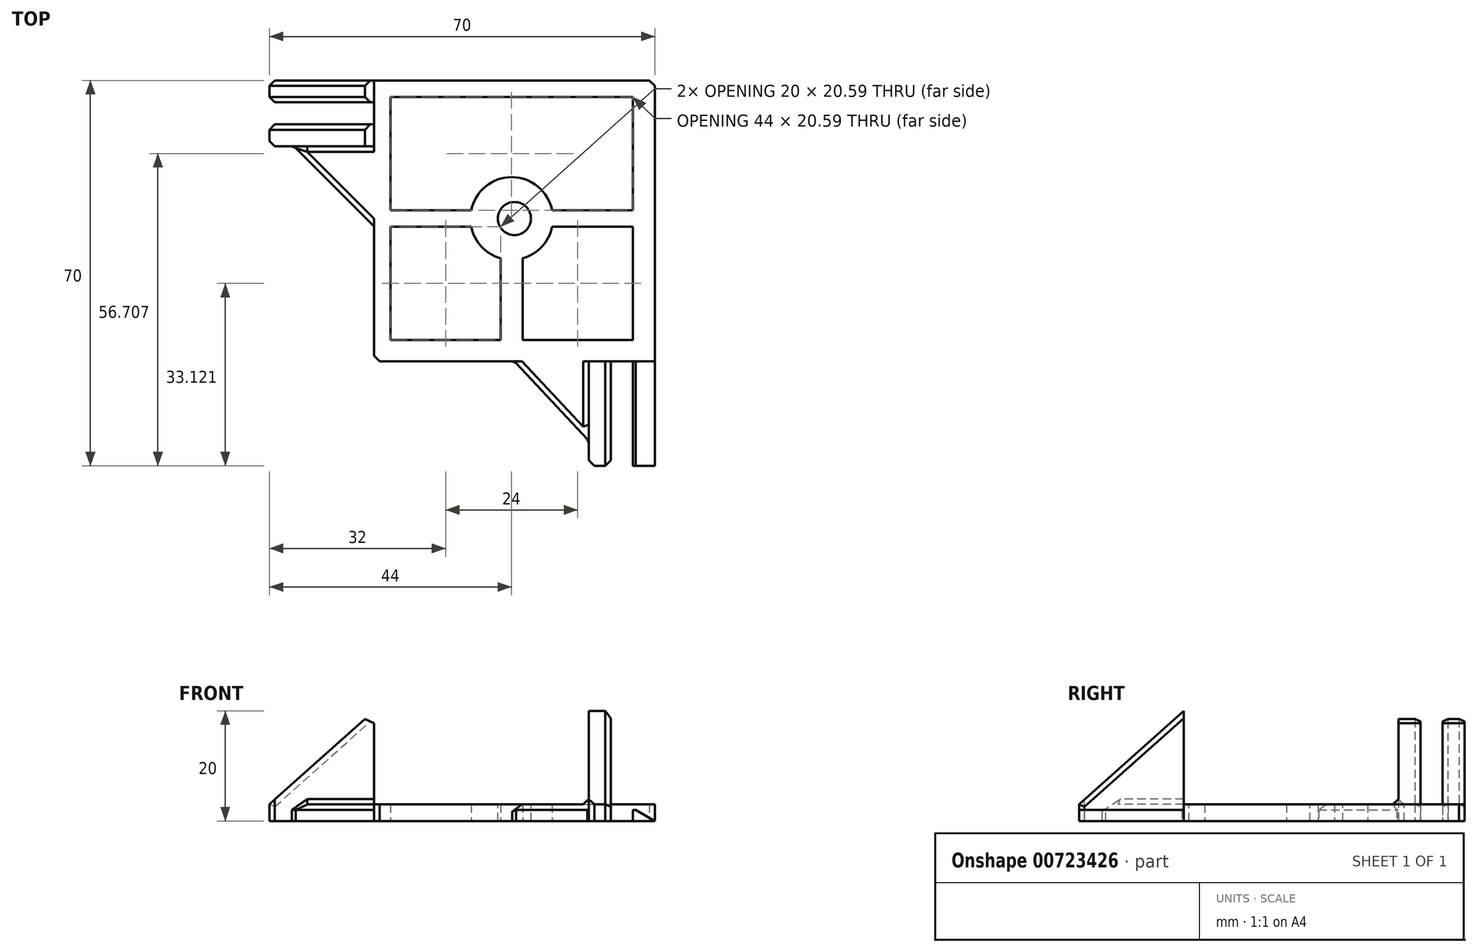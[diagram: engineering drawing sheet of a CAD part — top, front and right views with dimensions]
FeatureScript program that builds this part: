
annotation { "Feature Type Name" : "Feature", "Feature Type Description" : "" }
export const myFeature = defineFeature(function(context is Context, id is Id, definition is map)
    precondition{}
    {
        {
            var Q0;
            Q0=qCreatedBy(makeId("Top.planeOp"),FACE);
            var sketch = newSketch(context, id + "F0", { "sketchPlane" : qUnion([Q0])});
            skLineSegment(sketch, "E0.bottom", {"start": v(0, 0) * mm, "end": v(51, 0) * mm});
            skLineSegment(sketch, "E0.top", {"start": v(0, -51) * mm, "end": v(51, -51) * mm});
            skLineSegment(sketch, "E0.left", {"start": v(0, 0) * mm, "end": v(0, -51) * mm});
            skLineSegment(sketch, "E0.right", {"start": v(51, 0) * mm, "end": v(51, -51) * mm});
            skSolve(sketch);
        }
        {
            var Q0;
            Q0=qSketchRegion(id+"F0",true);
            extrude(context, id + "F1", {"entities" : qUnion([Q0]), "depth" : 3 * mm, "offsetDistance" : 25 * mm});
        }
        {
            var Q0;
            Q0=qCreatedBy(makeId("Top.planeOp"),FACE);
            var sketch = newSketch(context, id + "F2", { "sketchPlane" : qUnion([Q0])});
            skLineSegment(sketch, "E1", {"start": v(0, 0) * mm, "end": v(-19, 0) * mm});
            skLineSegment(sketch, "E2", {"start": v(-19, 0) * mm, "end": v(-19, -4) * mm});
            skLineSegment(sketch, "E3", {"start": v(-19, -4) * mm, "end": v(0, -4) * mm});
            skLineSegment(sketch, "E4", {"start": v(0, -4) * mm, "end": v(0, -8) * mm});
            skLineSegment(sketch, "E5", {"start": v(0, -8) * mm, "end": v(-19, -8) * mm});
            skLineSegment(sketch, "E6", {"start": v(-19, -8) * mm, "end": v(-19, -12) * mm});
            skLineSegment(sketch, "E7", {"start": v(-19, -12) * mm, "end": v(0, -12) * mm});
            skLineSegment(sketch, "E8", {"start": v(0, 0) * mm, "end": v(0, -12) * mm});
            skSolve(sketch);
        }
        {
            var Q0;
            Q0=qSketchRegion(id+"F2",true);
            extrude(context, id + "F3", {"entities" : qUnion([Q0]), "operationType" : NewBodyOperationType.ADD, "depth" : 20 * mm, "offsetDistance" : 25 * mm});
        }
        {
            var Q0;
            Q0=qCreatedBy(makeId("Top.planeOp"),FACE);
            var sketch = newSketch(context, id + "F4", { "sketchPlane" : qUnion([Q0])});
            skLineSegment(sketch, "E9", {"start": v(0, 0) * mm, "end": v(0, -11.5) * mm});
            skLineSegment(sketch, "E10", {"start": v(0, -11.5) * mm, "end": v(-15, -11.5) * mm});
            skLineSegment(sketch, "E11", {"start": v(0, -11.5) * mm, "end": v(0, -26.5) * mm});
            skLineSegment(sketch, "E12", {"start": v(0, -26.5) * mm, "end": v(-15, -11.5) * mm});
            skSolve(sketch);
        }
        {
            var Q0;
            Q0=makeQuery(id+"F4.imprint","IMPRINT",FACE,{"disambiguationData":[TD([[makeQuery(id+"F4.imprint","IMPRINT",EDGE,{"derivedFrom":sQuery(id+"F4.wireOp",EDGE,"E10")}),1.0]])]});
            extrude(context, id + "F5", {"entities" : qUnion([Q0]), "operationType" : NewBodyOperationType.ADD, "depth" : 3 * mm, "offsetDistance" : 25 * mm});
        }
        {
            var Q0;
            Q0=qCreatedBy(makeId("Top.planeOp"),FACE);
            var sketch = newSketch(context, id + "F6", { "sketchPlane" : qUnion([Q0])});
            skLineSegment(sketch, "E13", {"start": v(0, 0) * mm, "end": v(0, -51) * mm});
            skLineSegment(sketch, "E14", {"start": v(0, -51) * mm, "end": v(51, -51) * mm});
            skLineSegment(sketch, "E15", {"start": v(51, -51) * mm, "end": v(51, -70) * mm});
            skLineSegment(sketch, "E16", {"start": v(51, -70) * mm, "end": v(47, -70) * mm});
            skLineSegment(sketch, "E17", {"start": v(47, -70) * mm, "end": v(47, -51) * mm});
            skLineSegment(sketch, "E18", {"start": v(47, -51) * mm, "end": v(43, -51) * mm});
            skLineSegment(sketch, "E19", {"start": v(43, -51) * mm, "end": v(43, -70) * mm});
            skLineSegment(sketch, "E20", {"start": v(43, -70) * mm, "end": v(39, -70) * mm});
            skLineSegment(sketch, "E21", {"start": v(39, -70) * mm, "end": v(39, -51) * mm});
            skLineSegment(sketch, "E22", {"start": v(39, -51) * mm, "end": v(51, -51) * mm});
            skSolve(sketch);
        }
        {
            var Q0;
            Q0=qCreatedBy(makeId("Top.planeOp"),FACE);
            var sketch = newSketch(context, id + "F7", { "sketchPlane" : qUnion([Q0])});
            skLineSegment(sketch, "E23", {"start": v(0, 0) * mm, "end": v(0, -51) * mm});
            skLineSegment(sketch, "E24", {"start": v(0, -51) * mm, "end": v(51, -51) * mm});
            skLineSegment(sketch, "E25", {"start": v(51, -51) * mm, "end": v(39.5, -51) * mm});
            skLineSegment(sketch, "E26", {"start": v(39.5, -51) * mm, "end": v(39.5, -66) * mm});
            skLineSegment(sketch, "E27", {"start": v(39.5, -66) * mm, "end": v(25.5, -51) * mm});
            skLineSegment(sketch, "E28", {"start": v(25.5, -51) * mm, "end": v(39.5, -51) * mm});
            skSolve(sketch);
        }
        {
            var Q0;
            Q0=qSketchRegion(id+"F7",true);
            extrude(context, id + "F8", {"entities" : qUnion([Q0]), "operationType" : NewBodyOperationType.ADD, "depth" : 3 * mm, "offsetDistance" : 25 * mm});
        }
        {
            var Q0;
            Q0=makeQuery(id+"F8.opExtrude","CAP_EDGE",EDGE,{"disambiguationData":[OSD([sQuery(id+"F7.wireOp",EDGE,"E27")])],"isStart":false});
            chamfer(context, id + "F9", {"entities" : qUnion([Q0]), "width" : 1 * mm, "tangentPropagation" : true});
        }
        {
            var Q0;
            Q0=makeQuery(id+"F8.boolean.opBoolean","MERGE",FACE,{"derivedFrom":[makeQuery(id+"F5.boolean.opBoolean","MERGE",FACE,{"derivedFrom":[makeQuery(id+"F1.opExtrude","CAP_FACE",FACE,{"disambiguationData":[OSD([sQuery(id+"F0.wireOp",EDGE,"E0.bottom"),sQuery(id+"F0.wireOp",EDGE,"E0.top"),sQuery(id+"F0.wireOp",EDGE,"E0.left"),sQuery(id+"F0.wireOp",EDGE,"E0.right")])],"isStart":false}),makeQuery(id+"F5.opExtrude","CAP_FACE",FACE,{"disambiguationData":[OSD([sQuery(id+"F4.wireOp",EDGE,"E10"),sQuery(id+"F4.wireOp",EDGE,"E11"),sQuery(id+"F4.wireOp",EDGE,"E12")])],"isStart":false})]}),makeQuery(id+"F8.opExtrude","CAP_FACE",FACE,{"disambiguationData":[OSD([sQuery(id+"F7.wireOp",EDGE,"E26"),sQuery(id+"F7.wireOp",EDGE,"E27"),sQuery(id+"F7.wireOp",EDGE,"E28")])],"isStart":false})]});
            var sketch = newSketch(context, id + "F10", { "sketchPlane" : qUnion([Q0])});
            skCircle(sketch, "E29", {"center": v(25.5, -25.09) * mm, "radius": 3 * mm});
            skPoint(sketch, "E29.centerSnap0", {"position": v(25.5, 0) * mm});
            skSolve(sketch);
        }
        {
            var Q0;
            Q0=qSketchRegion(id+"F10",true);
            extrude(context, id + "F11", {"entities" : qUnion([Q0]), "operationType" : NewBodyOperationType.REMOVE, "oppositeDirection" : true, "depth" : 25 * mm, "offsetDistance" : 25 * mm});
        }
        {
            var Q0;
            {var subQ0=sQuery(id+"F6.wireOp",EDGE,"E19");Q0=makeQuery(id+"F6.imprint","IMPRINT",FACE,{"disambiguationData":[TD([[makeQuery(id+"F6.imprint","IMPRINT",EDGE,{"derivedFrom":subQ0}),-1.0]])]});}
            extrude(context, id + "F12", {"entities" : qUnion([Q0]), "operationType" : NewBodyOperationType.ADD, "depth" : 20 * mm, "offsetDistance" : 25 * mm});
        }
        {
            var Q0;
            Q0 = qSketchRegion(id + "F6", true);
            extrude(context, id + "F13", {"entities" : qUnion([Q0]), "operationType" : NewBodyOperationType.ADD, "depth" : 2 * mm, "offsetDistance" : 25 * mm});
        }
        {
            var Q0;
            Q0=makeQuery(id+"F13.opExtrude","CAP_EDGE",EDGE,{"disambiguationData":[OSD([sQuery(id+"F6.wireOp",EDGE,"E15")])],"isStart":false});
            chamfer(context, id + "F14", {"entities" : qUnion([Q0]), "chamferType" : ChamferType.OFFSET_ANGLE, "width" : 2 * mm, "oppositeDirection" : false, "angle" : 60 * degree});
        }
        {
            var Q0;
            Q0=qCreatedBy(makeId("Top.planeOp"),FACE);
            var sketch = newSketch(context, id + "F15", { "sketchPlane" : qUnion([Q0])});
            skCircle(sketch, "E30", {"center": v(25, -25.09) * mm, "radius": 7.5 * mm});
            skLineSegment(sketch, "E31", {"start": v(0, 0) * mm, "end": v(0, -3) * mm});
            skLineSegment(sketch, "E32", {"start": v(0, -3) * mm, "end": v(25, -3) * mm});
            skLineSegment(sketch, "E33", {"start": v(25, -3) * mm, "end": v(23, -3) * mm});
            skLineSegment(sketch, "E34", {"start": v(23, -3) * mm, "end": v(23, -17.86) * mm});
            skLineSegment(sketch, "E35", {"start": v(0, -3) * mm, "end": v(3, -3) * mm});
            skLineSegment(sketch, "E36", {"start": v(3, -3) * mm, "end": v(3, -25.09) * mm});
            skLineSegment(sketch, "E37", {"start": v(3, -25.09) * mm, "end": v(3, -23.59) * mm});
            skLineSegment(sketch, "E38", {"start": v(3, -23.59) * mm, "end": v(17.65, -23.59) * mm});
            skLineSegment(sketch, "E39", {"start": v(25, -25.09) * mm, "end": v(51, -25.09) * mm});
            skLineSegment(sketch, "E40", {"start": v(25, -25.09) * mm, "end": v(25, -51) * mm});
            skLineSegment(sketch, "E41.MirrorCS", {"start": v(3, -26.59) * mm, "end": v(17.65, -26.59) * mm});
            skLineSegment(sketch, "E42.MirrorCS", {"start": v(3, -47.17) * mm, "end": v(3, -25.09) * mm});
            skLineSegment(sketch, "E43.MirrorCS", {"start": v(0, -47.17) * mm, "end": v(25, -47.17) * mm});
            skLineSegment(sketch, "E44.MirrorCS", {"start": v(23, -47.17) * mm, "end": v(23, -32.31) * mm});
            skLineSegment(sketch, "E45.MirrorCS", {"start": v(27, -47.17) * mm, "end": v(27, -32.31) * mm});
            skLineSegment(sketch, "E46.MirrorCS", {"start": v(50, -47.17) * mm, "end": v(25, -47.17) * mm});
            skLineSegment(sketch, "E47.MirrorCS", {"start": v(47, -47.17) * mm, "end": v(47, -25.09) * mm});
            skLineSegment(sketch, "E48.MirrorCS", {"start": v(47, -26.59) * mm, "end": v(32.35, -26.59) * mm});
            skLineSegment(sketch, "E49.MirrorCS", {"start": v(47, -23.59) * mm, "end": v(32.35, -23.59) * mm});
            skLineSegment(sketch, "E50.MirrorCS", {"start": v(47, -3) * mm, "end": v(47, -25.09) * mm});
            skLineSegment(sketch, "E51.MirrorCS", {"start": v(50, -3) * mm, "end": v(25, -3) * mm});
            skLineSegment(sketch, "E52.MirrorCS", {"start": v(27, -3) * mm, "end": v(27, -17.86) * mm});
            skLineSegment(sketch, "E53", {"start": v(0, 0) * mm, "end": v(0, -47.17) * mm});
            skSolve(sketch);
        }
        {
            var Q0;
            {var subQ4=sQuery(id+"F15.wireOp",EDGE,"E49.MirrorCS");Q0=makeQuery(id+"F15.imprint","IMPRINT",FACE,{"disambiguationData":[TD([[makeQuery(id+"F15.imprint","IMPRINT",EDGE,{"derivedFrom":subQ4}),-1.0]])]});}
            var Q1;
            {var subQ4=sQuery(id+"F15.wireOp",EDGE,"E45.MirrorCS");Q1=makeQuery(id+"F15.imprint","IMPRINT",FACE,{"disambiguationData":[TD([[makeQuery(id+"F15.imprint","IMPRINT",EDGE,{"derivedFrom":subQ4}),-1.0]])]});}
            var Q2;
            {var subQ1=sQuery(id+"F15.wireOp",EDGE,"E41.MirrorCS");Q2=makeQuery(id+"F15.imprint","IMPRINT",FACE,{"disambiguationData":[TD([[makeQuery(id+"F15.imprint","IMPRINT",EDGE,{"derivedFrom":subQ1}),-1.0]])]});}
            var Q3;
            Q3=makeQuery(id+"F15.imprint","IMPRINT",FACE,{"disambiguationData":[TD([[makeQuery(id+"F15.imprint","IMPRINT",EDGE,{"derivedFrom":sQuery(id+"F15.wireOp",EDGE,"E32")}),-1.0]])]});
            extrude(context, id + "F16", {"entities" : qUnion([Q0, Q1, Q2, Q3]), "operationType" : NewBodyOperationType.REMOVE, "depth" : 25 * mm, "offsetDistance" : 25 * mm});
        }
        {
            var Q0;
            Q0=makeQuery(id+"F3.opExtrude","SWEPT_FACE",FACE,{"disambiguationData":[OSD([sQuery(id+"F2.wireOp",EDGE,"E7")])]});
            var sketch = newSketch(context, id + "F17", { "sketchPlane" : qUnion([Q0])});
            skLineSegment(sketch, "E54", {"start": v(-19, 20) * mm, "end": v(-19, 3) * mm});
            skLineSegment(sketch, "E55", {"start": v(-19, 3) * mm, "end": v(0, 3) * mm});
            skLineSegment(sketch, "E56", {"start": v(-19, 20) * mm, "end": v(0, 20) * mm});
            skLineSegment(sketch, "E57", {"start": v(0, 20) * mm, "end": v(-19, 3) * mm});
            skSolve(sketch);
        }
        {
            var Q0;
            Q0 = qSketchRegion(id + "F17", true);
            extrude(context, id + "F18", {"entities" : qUnion([Q0]), "operationType" : NewBodyOperationType.REMOVE, "oppositeDirection" : true, "depth" : 25 * mm, "offsetDistance" : 25 * mm});
        }
        {
            var Q0;
            Q0=makeQuery(id+"F12.opExtrude","SWEPT_FACE",FACE,{"disambiguationData":[OSD([sQuery(id+"F6.wireOp",EDGE,"E21")])]});
            var sketch = newSketch(context, id + "F19", { "sketchPlane" : qUnion([Q0])});
            skLineSegment(sketch, "E58", {"start": v(51, 3) * mm, "end": v(70, 3) * mm});
            skLineSegment(sketch, "E59", {"start": v(70, 3) * mm, "end": v(51, 20) * mm});
            skLineSegment(sketch, "E60", {"start": v(51, 20) * mm, "end": v(70, 20) * mm});
            skLineSegment(sketch, "E61", {"start": v(70, 20) * mm, "end": v(70, 3) * mm});
            skSolve(sketch);
        }
        {
            var Q0;
            Q0 = qSketchRegion(id + "F19", true);
            extrude(context, id + "F20", {"entities" : qUnion([Q0]), "operationType" : NewBodyOperationType.REMOVE, "oppositeDirection" : true, "depth" : 25 * mm, "offsetDistance" : 25 * mm});
        }
        {
            var Q0;
            Q0=makeQuery(id+"F18.boolean.opBoolean","INTERSECT",EDGE,{"derivedFrom":[makeQuery(id+"F3.boolean.opBoolean","MERGE",FACE,{"derivedFrom":[makeQuery(id+"F1.opExtrude","SWEPT_FACE",FACE,{"disambiguationData":[OSD([sQuery(id+"F0.wireOp",EDGE,"E0.bottom")])]}),makeQuery(id+"F3.opExtrude","SWEPT_FACE",FACE,{"disambiguationData":[OSD([sQuery(id+"F2.wireOp",EDGE,"E1")])]})]}),makeQuery(id+"F18.opExtrude","SWEPT_FACE",FACE,{"disambiguationData":[OSD([sQuery(id+"F17.wireOp",EDGE,"E57")])]})]});
            var Q1;
            Q1=makeQuery(id+"F18.boolean.opBoolean","INTERSECT",EDGE,{"derivedFrom":[makeQuery(id+"F3.opExtrude","SWEPT_FACE",FACE,{"disambiguationData":[OSD([sQuery(id+"F2.wireOp",EDGE,"E3")])]}),makeQuery(id+"F18.opExtrude","SWEPT_FACE",FACE,{"disambiguationData":[OSD([sQuery(id+"F17.wireOp",EDGE,"E57")])]})]});
            var Q2;
            Q2=makeQuery(id+"F18.boolean.opBoolean","INTERSECT",EDGE,{"derivedFrom":[makeQuery(id+"F3.opExtrude","SWEPT_FACE",FACE,{"disambiguationData":[OSD([sQuery(id+"F2.wireOp",EDGE,"E5")])]}),makeQuery(id+"F18.opExtrude","SWEPT_FACE",FACE,{"disambiguationData":[OSD([sQuery(id+"F17.wireOp",EDGE,"E57")])]})]});
            var Q3;
            Q3=makeQuery(id+"F18.boolean.opBoolean","COPY",EDGE,{"derivedFrom":makeQuery(id+"F18.opExtrude","CAP_EDGE",EDGE,{"disambiguationData":[OSD([sQuery(id+"F17.wireOp",EDGE,"E57")])],"isStart":true})});
            var Q4;
            Q4=makeQuery(id+"F5.opExtrude","CAP_EDGE",EDGE,{"disambiguationData":[OSD([sQuery(id+"F4.wireOp",EDGE,"E12")])],"isStart":false});
            var Q5;
            Q5=makeQuery(id+"F20.boolean.opBoolean","COPY",EDGE,{"derivedFrom":makeQuery(id+"F20.opExtrude","CAP_EDGE",EDGE,{"disambiguationData":[OSD([sQuery(id+"F19.wireOp",EDGE,"E59")])],"isStart":true})});
            var Q6;
            Q6=makeQuery(id+"F20.boolean.opBoolean","INTERSECT",EDGE,{"derivedFrom":[makeQuery(id+"F12.opExtrude","SWEPT_FACE",FACE,{"disambiguationData":[OSD([sQuery(id+"F6.wireOp",EDGE,"E19")])]}),makeQuery(id+"F20.opExtrude","SWEPT_FACE",FACE,{"disambiguationData":[OSD([sQuery(id+"F19.wireOp",EDGE,"E59")])]})]});
            var Q7;
            {var subQ0=sQuery(id+"F2.wireOp",EDGE,"E8");Q7=makeQuery(id+"F18.boolean.opBoolean","MERGE",EDGE,{"derivedFrom":[makeQuery(id+"F3.opExtrude","CAP_EDGE",EDGE,{"disambiguationData":[OSD([subQ0]),TDD([makeQuery(id+"F2.imprint","IMPRINT",EDGE,{"disambiguationData":[TD([[makeQuery(id+"F2.imprint","INTERSECT",VERTEX,{"derivedFrom":[sQuery(id+"F2.wireOp",EDGE,"E1"),subQ0]}),-1.0]])],"derivedFrom":subQ0})])],"isStart":false}),makeQuery(id+"F18.opExtrude","SWEPT_EDGE",EDGE,{"disambiguationData":[OSD([sQuery(id+"F2.wireOp",EDGE,"E7"),subQ0,sQuery(id+"F17.wireOp",EDGE,"E56"),sQuery(id+"F17.wireOp",EDGE,"E57")])]})]});}
            var Q8;
            {var subQ0=sQuery(id+"F2.wireOp",EDGE,"E8");var subQ1=sQuery(id+"F2.wireOp",EDGE,"E7");Q8=makeQuery(id+"F18.boolean.opBoolean","MERGE",EDGE,{"derivedFrom":[makeQuery(id+"F3.opExtrude","CAP_EDGE",EDGE,{"disambiguationData":[OSD([subQ0]),TDD([makeQuery(id+"F2.imprint","IMPRINT",EDGE,{"disambiguationData":[TD([[makeQuery(id+"F2.imprint","INTERSECT",VERTEX,{"derivedFrom":[sQuery(id+"F2.wireOp",EDGE,"E5"),subQ0]}),-1.0]])],"derivedFrom":subQ0})])],"isStart":false}),makeQuery(id+"F18.opExtrude","SWEPT_EDGE",EDGE,{"disambiguationData":[OSD([subQ1,subQ0,sQuery(id+"F17.wireOp",EDGE,"E56"),sQuery(id+"F17.wireOp",EDGE,"E57")])]})]});}
            var Q9;
            {var subQ0=sQuery(id+"F6.wireOp",EDGE,"E22");Q9=makeQuery(id+"F20.boolean.opBoolean","MERGE",EDGE,{"derivedFrom":[makeQuery(id+"F12.opExtrude","CAP_EDGE",EDGE,{"disambiguationData":[OSD([subQ0])],"isStart":false}),makeQuery(id+"F20.opExtrude","SWEPT_EDGE",EDGE,{"disambiguationData":[OSD([sQuery(id+"F6.wireOp",EDGE,"E21"),subQ0,sQuery(id+"F19.wireOp",EDGE,"E59"),sQuery(id+"F19.wireOp",EDGE,"E60")])]})]});}
            var Q10;
            {var subQ0=sQuery(id+"F17.wireOp",EDGE,"E57");Q10=makeQuery(id+"F18.boolean.opBoolean","COPY",EDGE,{"disambiguationData":[topologyDisambiguationEdgeConnected([makeQuery(id+"F3.opExtrude","SWEPT_FACE",FACE,{"disambiguationData":[OSD([sQuery(id+"F2.wireOp",EDGE,"E2")])]})])],"derivedFrom":makeQuery(id+"F18.opExtrude","SWEPT_EDGE",EDGE,{"disambiguationData":[OSD([sQuery(id+"F2.wireOp",EDGE,"E6"),sQuery(id+"F2.wireOp",EDGE,"E7"),sQuery(id+"F17.wireOp",EDGE,"E54"),sQuery(id+"F17.wireOp",EDGE,"E55"),subQ0])]})});}
            var Q11;
            {var subQ0=sQuery(id+"F2.wireOp",EDGE,"E6");var subQ1=sQuery(id+"F17.wireOp",EDGE,"E57");Q11=makeQuery(id+"F18.boolean.opBoolean","COPY",EDGE,{"disambiguationData":[topologyDisambiguationEdgeConnected([makeQuery(id+"F3.opExtrude","SWEPT_FACE",FACE,{"disambiguationData":[OSD([subQ0])]})])],"derivedFrom":makeQuery(id+"F18.opExtrude","SWEPT_EDGE",EDGE,{"disambiguationData":[OSD([subQ0,sQuery(id+"F2.wireOp",EDGE,"E7"),sQuery(id+"F17.wireOp",EDGE,"E54"),sQuery(id+"F17.wireOp",EDGE,"E55"),subQ1])]})});}
            var Q12;
            Q12=makeQuery(id+"F20.boolean.opBoolean","COPY",EDGE,{"derivedFrom":makeQuery(id+"F20.opExtrude","SWEPT_EDGE",EDGE,{"disambiguationData":[OSD([sQuery(id+"F6.wireOp",EDGE,"E20"),sQuery(id+"F6.wireOp",EDGE,"E21"),sQuery(id+"F19.wireOp",EDGE,"E58"),sQuery(id+"F19.wireOp",EDGE,"E59"),sQuery(id+"F19.wireOp",EDGE,"E61")])]})});
            var Q13;
            Q13=makeQuery(id+"F5.boolean.opBoolean","INTERSECT",EDGE,{"derivedFrom":[makeQuery(id+"F3.opExtrude","SWEPT_FACE",FACE,{"disambiguationData":[OSD([sQuery(id+"F2.wireOp",EDGE,"E7")])]}),makeQuery(id+"F5.opExtrude","CAP_FACE",FACE,{"disambiguationData":[OSD([sQuery(id+"F4.wireOp",EDGE,"E10"),sQuery(id+"F4.wireOp",EDGE,"E11"),sQuery(id+"F4.wireOp",EDGE,"E12")])],"isStart":false})]});
            var Q14;
            Q14=makeQuery(id+"F12.boolean.opBoolean","INTERSECT",EDGE,{"derivedFrom":[makeQuery(id+"F8.boolean.opBoolean","MERGE",FACE,{"derivedFrom":[makeQuery(id+"F5.boolean.opBoolean","MERGE",FACE,{"derivedFrom":[makeQuery(id+"F1.opExtrude","CAP_FACE",FACE,{"disambiguationData":[OSD([sQuery(id+"F0.wireOp",EDGE,"E0.bottom"),sQuery(id+"F0.wireOp",EDGE,"E0.top"),sQuery(id+"F0.wireOp",EDGE,"E0.left"),sQuery(id+"F0.wireOp",EDGE,"E0.right")])],"isStart":false}),makeQuery(id+"F5.opExtrude","CAP_FACE",FACE,{"disambiguationData":[OSD([sQuery(id+"F4.wireOp",EDGE,"E10"),sQuery(id+"F4.wireOp",EDGE,"E11"),sQuery(id+"F4.wireOp",EDGE,"E12")])],"isStart":false})]}),makeQuery(id+"F8.opExtrude","CAP_FACE",FACE,{"disambiguationData":[OSD([sQuery(id+"F7.wireOp",EDGE,"E26"),sQuery(id+"F7.wireOp",EDGE,"E27"),sQuery(id+"F7.wireOp",EDGE,"E28")])],"isStart":false})]}),makeQuery(id+"F12.opExtrude","SWEPT_FACE",FACE,{"disambiguationData":[OSD([sQuery(id+"F6.wireOp",EDGE,"E21")])]})]});
            chamfer(context, id + "F21", {"entities" : qUnion([Q0, Q1, Q2, Q3, Q4, Q5, Q6, Q7, Q8, Q9, Q10, Q11, Q12, Q13, Q14]), "width" : 1 * mm, "tangentPropagation" : true});
        }
        {
            var Q0;
            Q0=makeQuery(id+"F1.opExtrude","SWEPT_EDGE",EDGE,{"disambiguationData":[OSD([sQuery(id+"F0.wireOp",EDGE,"E0.top"),sQuery(id+"F0.wireOp",EDGE,"E0.left")])]});
            var Q1;
            Q1=makeQuery(id+"F8.opExtrude","SWEPT_EDGE",EDGE,{"disambiguationData":[OSD([sQuery(id+"F7.wireOp",EDGE,"E27"),sQuery(id+"F7.wireOp",EDGE,"E28")])]});
            var Q2;
            Q2=makeQuery(id+"F12.boolean.opBoolean","INTERSECT",EDGE,{"derivedFrom":[makeQuery(id+"F8.opExtrude","SWEPT_FACE",FACE,{"disambiguationData":[OSD([sQuery(id+"F7.wireOp",EDGE,"E27")])]}),makeQuery(id+"F12.opExtrude","SWEPT_FACE",FACE,{"disambiguationData":[OSD([sQuery(id+"F6.wireOp",EDGE,"E21")])]})]});
            var Q3;
            Q3=makeQuery(id+"F5.opExtrude","SWEPT_EDGE",EDGE,{"disambiguationData":[OSD([sQuery(id+"F4.wireOp",EDGE,"E11"),sQuery(id+"F4.wireOp",EDGE,"E12")])]});
            var Q4;
            Q4=makeQuery(id+"F1.opExtrude","SWEPT_EDGE",EDGE,{"disambiguationData":[OSD([sQuery(id+"F0.wireOp",EDGE,"E0.bottom"),sQuery(id+"F0.wireOp",EDGE,"E0.right")])]});
            var Q5;
            Q5=makeQuery(id+"F3.opExtrude","SWEPT_EDGE",EDGE,{"disambiguationData":[OSD([sQuery(id+"F2.wireOp",EDGE,"E1"),sQuery(id+"F2.wireOp",EDGE,"E2")])]});
            var Q6;
            Q6=makeQuery(id+"F3.opExtrude","SWEPT_EDGE",EDGE,{"disambiguationData":[OSD([sQuery(id+"F2.wireOp",EDGE,"E2"),sQuery(id+"F2.wireOp",EDGE,"E3")])]});
            var Q7;
            Q7=makeQuery(id+"F3.opExtrude","SWEPT_EDGE",EDGE,{"disambiguationData":[OSD([sQuery(id+"F2.wireOp",EDGE,"E5"),sQuery(id+"F2.wireOp",EDGE,"E6")])]});
            var Q8;
            Q8=makeQuery(id+"F3.opExtrude","SWEPT_EDGE",EDGE,{"disambiguationData":[OSD([sQuery(id+"F2.wireOp",EDGE,"E6"),sQuery(id+"F2.wireOp",EDGE,"E7")])]});
            var Q9;
            Q9=makeQuery(id+"F12.opExtrude","SWEPT_EDGE",EDGE,{"disambiguationData":[OSD([sQuery(id+"F6.wireOp",EDGE,"E20"),sQuery(id+"F6.wireOp",EDGE,"E21")])]});
            var Q10;
            Q10=makeQuery(id+"F12.opExtrude","SWEPT_EDGE",EDGE,{"disambiguationData":[OSD([sQuery(id+"F6.wireOp",EDGE,"E19"),sQuery(id+"F6.wireOp",EDGE,"E20")])]});
            chamfer(context, id + "F22", {"entities" : qUnion([Q0, Q1, Q2, Q3, Q4, Q5, Q6, Q7, Q8, Q9, Q10]), "width" : 1 * mm, "tangentPropagation" : true});
        }
    });
